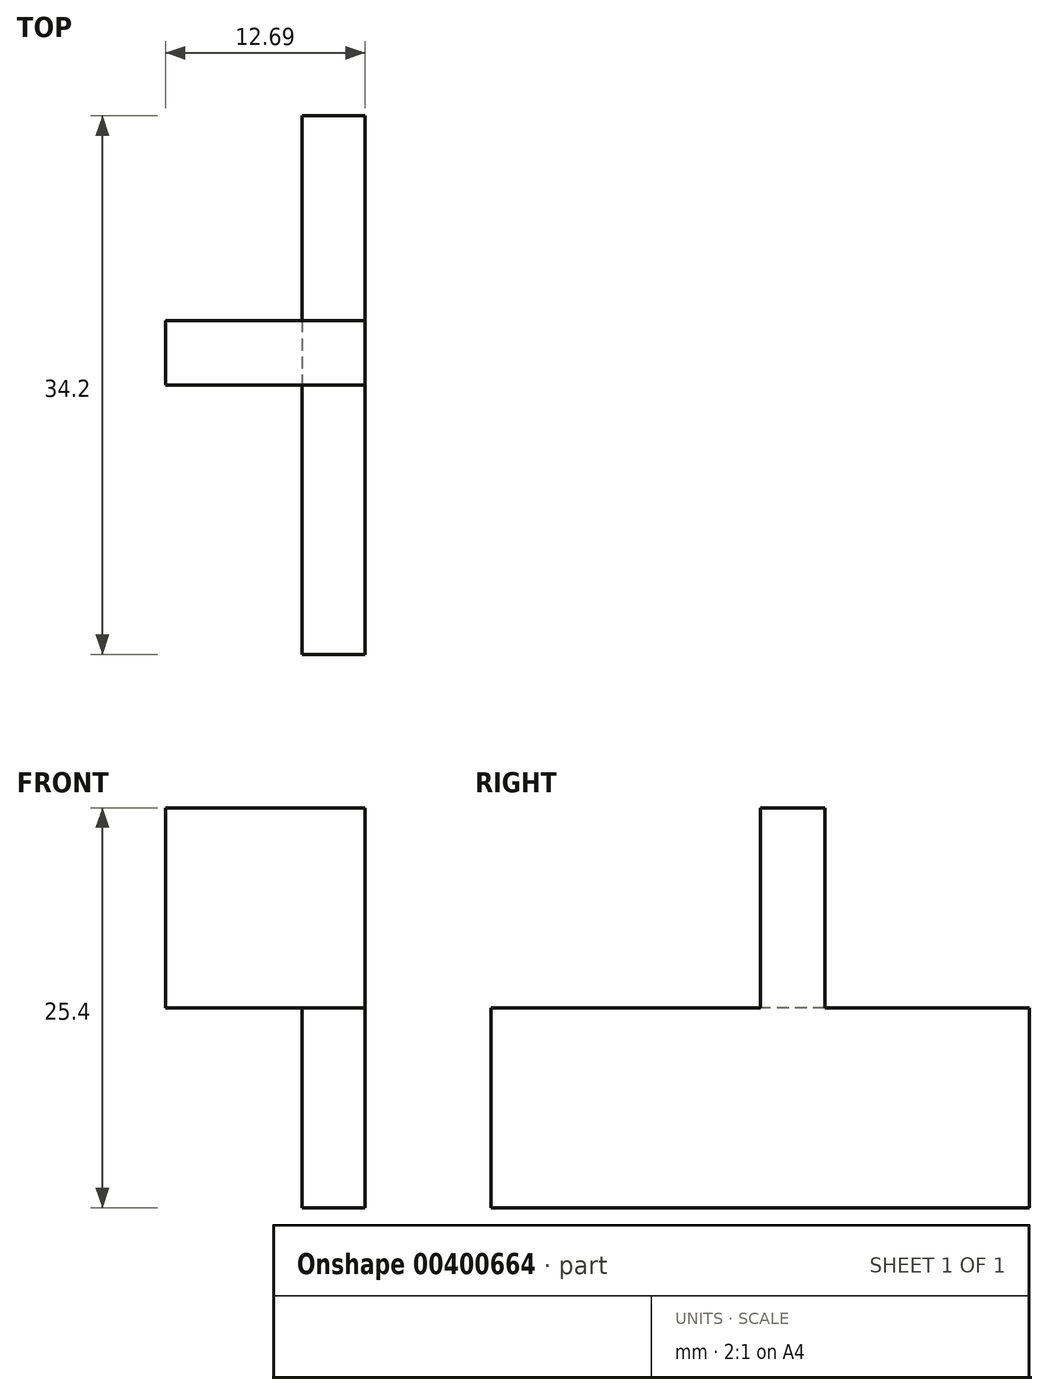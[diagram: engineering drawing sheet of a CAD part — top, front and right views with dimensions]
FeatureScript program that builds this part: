
annotation { "Feature Type Name" : "Feature", "Feature Type Description" : "" }
export const myFeature = defineFeature(function(context is Context, id is Id, definition is map)
    precondition{}
    {
        {
            var Q0;
            Q0=qCreatedBy(makeId("Top.planeOp"),FACE);
            var sketch = newSketch(context, id + "F0", { "sketchPlane" : qUnion([Q0])});
            skLineSegment(sketch, "E0.bottom", {"start": v(0, 34.2) * mm, "end": v(4.02, 34.2) * mm});
            skLineSegment(sketch, "E0.top", {"start": v(0, 0) * mm, "end": v(4.02, 0) * mm});
            skLineSegment(sketch, "E0.left", {"start": v(0, 34.2) * mm, "end": v(0, 0) * mm});
            skLineSegment(sketch, "E0.right", {"start": v(4.02, 34.2) * mm, "end": v(4.02, 0) * mm});
            skPoint(sketch, "E1.oppositeSnap0", {"position": v(4.02, 17.1) * mm});
            skLineSegment(sketch, "E1.bottom", {"start": v(-9.9, 19.65) * mm, "end": v(14.86, 19.65) * mm});
            skLineSegment(sketch, "E1.top", {"start": v(-9.9, 17.1) * mm, "end": v(14.86, 17.1) * mm});
            skLineSegment(sketch, "E1.left", {"start": v(-9.9, 19.65) * mm, "end": v(-9.9, 17.1) * mm});
            skLineSegment(sketch, "E1.right", {"start": v(14.86, 19.65) * mm, "end": v(14.86, 17.1) * mm});
            skSolve(sketch);
        }
        {
            var Q0;
            {var subQ0=sQuery(id+"F0.wireOp",EDGE,"E0.bottom");Q0=makeQuery(id+"F0.imprint","IMPRINT",FACE,{"disambiguationData":[TD([[makeQuery(id+"F0.imprint","IMPRINT",EDGE,{"derivedFrom":subQ0}),-1.0]])]});}
            var Q1;
            {var subQ0=sQuery(id+"F0.wireOp",EDGE,"E1.bottom");var subQ1=sQuery(id+"F0.wireOp",EDGE,"E0.left");var subQ2=makeQuery(id+"F0.imprint","INTERSECT",VERTEX,{"derivedFrom":[subQ1,subQ0]});Q1=makeQuery(id+"F0.imprint","IMPRINT",FACE,{"disambiguationData":[TD([[makeQuery(id+"F0.imprint","IMPRINT",EDGE,{"disambiguationData":[TD([[subQ2,-1.0]])],"derivedFrom":subQ1}),1.0]])]});}
            var Q2;
            {var subQ0=sQuery(id+"F0.wireOp",EDGE,"E0.top");Q2=makeQuery(id+"F0.imprint","IMPRINT",FACE,{"disambiguationData":[TD([[makeQuery(id+"F0.imprint","IMPRINT",EDGE,{"derivedFrom":subQ0}),1.0]])]});}
            extrude(context, id + "F1", {"entities" : qUnion([Q0, Q1, Q2]), "depth" : 12.7 * mm});
        }
        {
            var Q0;
            Q0=makeQuery(id+"F1.opExtrude","CAP_FACE",FACE,{"disambiguationData":[OSD([sQuery(id+"F0.wireOp",EDGE,"E0.bottom"),sQuery(id+"F0.wireOp",EDGE,"E0.top"),sQuery(id+"F0.wireOp",EDGE,"E0.left"),sQuery(id+"F0.wireOp",EDGE,"E0.right")])],"isStart":false});
            var sketch = newSketch(context, id + "F2", { "sketchPlane" : qUnion([Q0])});
            skPoint(sketch, "E2.firstSnap0", {"position": v(0, 17.1) * mm});
            skLineSegment(sketch, "E2.bottom", {"start": v(-8.67, 17.1) * mm, "end": v(12.7, 17.1) * mm});
            skLineSegment(sketch, "E2.top", {"start": v(-8.67, 21.2) * mm, "end": v(12.7, 21.2) * mm});
            skLineSegment(sketch, "E2.left", {"start": v(-8.67, 17.1) * mm, "end": v(-8.67, 21.2) * mm});
            skLineSegment(sketch, "E2.right", {"start": v(12.7, 17.1) * mm, "end": v(12.7, 21.2) * mm});
            skSolve(sketch);
        }
        {
            var Q0;
            {var subQ0=sQuery(id+"F2.wireOp",EDGE,"E2.left");Q0=makeQuery(id+"F2.imprint","IMPRINT",FACE,{"disambiguationData":[TD([[makeQuery(id+"F2.imprint","IMPRINT",EDGE,{"derivedFrom":subQ0}),-1.0]])]});}
            var Q1;
            {var subQ0=sQuery(id+"F2.wireOp",EDGE,"E2.bottom");var subQ1=makeQuery(id+"F1.opExtrude","CAP_EDGE",EDGE,{"disambiguationData":[OSD([sQuery(id+"F0.wireOp",EDGE,"E0.left")])],"isStart":false});var subQ2=makeQuery(id+"F2.imprint","INTERSECT",VERTEX,{"derivedFrom":[subQ1,subQ0]});Q1=makeQuery(id+"F2.imprint","IMPRINT",FACE,{"disambiguationData":[TD([[makeQuery(id+"F2.imprint","IMPRINT",EDGE,{"disambiguationData":[TD([[subQ2,-1.0]])],"derivedFrom":subQ0}),1.0]])]});}
            extrude(context, id + "F3", {"entities" : qUnion([Q0, Q1]), "operationType" : NewBodyOperationType.ADD, "depth" : 12.7 * mm});
        }
    });
